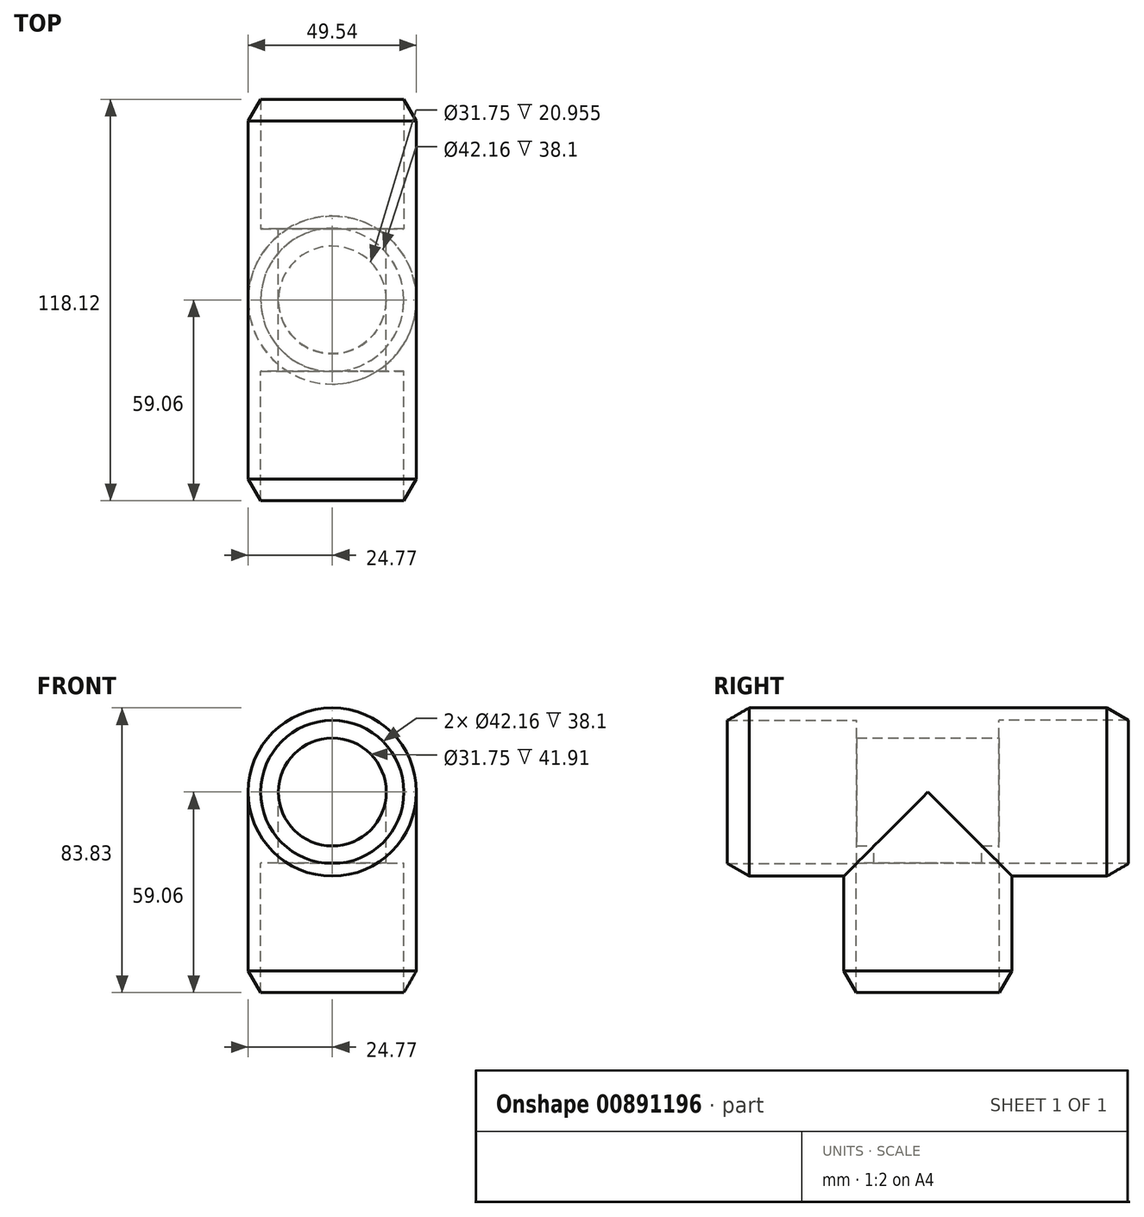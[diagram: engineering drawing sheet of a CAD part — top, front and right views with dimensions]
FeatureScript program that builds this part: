
annotation { "Feature Type Name" : "Feature", "Feature Type Description" : "" }
export const myFeature = defineFeature(function(context is Context, id is Id, definition is map)
    precondition{}
    {
        {
            var Q0;
            Q0=qCreatedBy(makeId("Right.planeOp"),FACE);
            var sketch = newSketch(context, id + "F0", { "sketchPlane" : qUnion([Q0])});
            skLineSegment(sketch, "E0", {"start": v(-59.06, 21.08) * mm, "end": v(-20.96, 21.08) * mm});
            skLineSegment(sketch, "E1", {"start": v(-20.96, 21.08) * mm, "end": v(-20.96, 15.88) * mm});
            skLineSegment(sketch, "E2", {"start": v(-20.96, 15.88) * mm, "end": v(0, 15.88) * mm});
            skLineSegment(sketch, "E3", {"start": v(15.87, 0) * mm, "end": v(15.87, 0) * mm});
            skLineSegment(sketch, "E4", {"start": v(15.87, 0) * mm, "end": v(24.77, 0) * mm});
            skLineSegment(sketch, "E5", {"start": v(24.77, 0) * mm, "end": v(24.77, 0) * mm});
            skLineSegment(sketch, "E6", {"start": v(0, 24.77) * mm, "end": v(-52.68, 24.76) * mm});
            skLineSegment(sketch, "E7", {"start": v(-52.68, 24.76) * mm, "end": v(-59.06, 21.08) * mm});
            skArc(sketch, "E8.filletArc", {"start": v(24.77, 0) * mm, "mid": v(17.51, 17.51) * mm, "end": v(0, 24.77) * mm});
            skArc(sketch, "E9.filletArc", {"start": v(15.88, 0) * mm, "mid": v(11.23, 11.23) * mm, "end": v(0, 15.88) * mm});
            skLineSegment(sketch, "E10", {"start": v(0, 0) * mm, "end": v(0, -11.7) * mm});
            skLineSegment(sketch, "E11", {"start": v(0, 0) * mm, "end": v(10.52, 0) * mm});
            skLineSegment(sketch, "E12", {"start": v(-59.06, 21.08) * mm, "end": v(-59.06, 0) * mm});
            skLineSegment(sketch, "E13", {"start": v(-59.06, 0) * mm, "end": v(15.87, 0) * mm});
            skSolve(sketch);
        }
        {
            var Q0;
            Q0=qCreatedBy(makeId("Right.planeOp"),FACE);
            var sketch = newSketch(context, id + "F1", { "sketchPlane" : qUnion([Q0])});
            skLineSegment(sketch, "E14", {"start": v(-21.08, -59.06) * mm, "end": v(-21.08, -20.96) * mm});
            skLineSegment(sketch, "E15", {"start": v(-21.08, -20.96) * mm, "end": v(-15.88, -20.96) * mm});
            skLineSegment(sketch, "E16", {"start": v(-15.88, -20.96) * mm, "end": v(-15.88, 0) * mm});
            skLineSegment(sketch, "E17", {"start": v(0, 15.88) * mm, "end": v(0, 15.88) * mm});
            skLineSegment(sketch, "E18", {"start": v(0, 15.88) * mm, "end": v(0, 24.77) * mm});
            skLineSegment(sketch, "E19", {"start": v(0, 24.77) * mm, "end": v(0, 24.77) * mm});
            skLineSegment(sketch, "E20", {"start": v(-24.77, 0) * mm, "end": v(-24.76, -52.68) * mm});
            skLineSegment(sketch, "E21", {"start": v(-24.76, -52.68) * mm, "end": v(-21.08, -59.06) * mm});
            skArc(sketch, "E22.filletArc", {"start": v(0, 24.77) * mm, "mid": v(-17.51, 17.51) * mm, "end": v(-24.77, 0) * mm});
            skArc(sketch, "E23.filletArc", {"start": v(0, 15.88) * mm, "mid": v(-11.23, 11.23) * mm, "end": v(-15.88, 0) * mm});
            skLineSegment(sketch, "E24", {"start": v(0, 36.04) * mm, "end": v(0, 0) * mm});
            skLineSegment(sketch, "E25", {"start": v(-2.18, 0) * mm, "end": v(0, 0) * mm});
            skLineSegment(sketch, "E26", {"start": v(-21.08, -59.06) * mm, "end": v(0, -59.06) * mm});
            skLineSegment(sketch, "E27", {"start": v(0, -59.06) * mm, "end": v(0, 15.88) * mm});
            skSolve(sketch);
        }
        {
            var Q0;
            Q0=qCreatedBy(makeId("Right.planeOp"),FACE);
            var sketch = newSketch(context, id + "F2", { "sketchPlane" : qUnion([Q0])});
            skLineSegment(sketch, "E28", {"start": v(59.06, -21.08) * mm, "end": v(20.96, -21.08) * mm});
            skLineSegment(sketch, "E29", {"start": v(20.96, -21.08) * mm, "end": v(20.96, -15.88) * mm});
            skLineSegment(sketch, "E30", {"start": v(20.96, -15.88) * mm, "end": v(0, -15.88) * mm});
            skLineSegment(sketch, "E31", {"start": v(-15.87, 0) * mm, "end": v(-15.87, 0) * mm});
            skLineSegment(sketch, "E32", {"start": v(-15.87, 0) * mm, "end": v(-24.77, 0) * mm});
            skLineSegment(sketch, "E33", {"start": v(-24.77, 0) * mm, "end": v(-24.77, 0) * mm});
            skLineSegment(sketch, "E34", {"start": v(0, -24.77) * mm, "end": v(52.68, -24.76) * mm});
            skLineSegment(sketch, "E35", {"start": v(52.68, -24.77) * mm, "end": v(59.06, -21.08) * mm});
            skArc(sketch, "E36.filletArc", {"start": v(-24.77, 0) * mm, "mid": v(-17.51, -17.51) * mm, "end": v(0, -24.77) * mm});
            skArc(sketch, "E37.filletArc", {"start": v(-15.88, 0) * mm, "mid": v(-11.23, -11.23) * mm, "end": v(0, -15.88) * mm});
            skLineSegment(sketch, "E38", {"start": v(0, 2.6) * mm, "end": v(0, 0) * mm});
            skLineSegment(sketch, "E39", {"start": v(0, 0) * mm, "end": v(10.52, 0) * mm});
            skLineSegment(sketch, "E40", {"start": v(59.06, -21.08) * mm, "end": v(59.06, 0) * mm});
            skLineSegment(sketch, "E41", {"start": v(59.06, 0) * mm, "end": v(-15.87, 0) * mm});
            skSolve(sketch);
        }
        {
            var Q0;
            Q0=qSketchRegion(id+"F0",true);
            var Q1;
            Q1=sQuery(id+"F0.wireOp",EDGE,"E13");
            revolve(context, id + "F3", {"surfaceOperationType" : NewSurfaceOperationType.NEW, "entities" : qUnion([Q0]), "axis" : qUnion([Q1]), "revolveType" : RevolveType.FULL});
        }
        {
            var Q0;
            Q0=qSketchRegion(id+"F1",true);
            var Q1;
            Q1=sQuery(id+"F1.wireOp",EDGE,"E27");
            revolve(context, id + "F4", {"operationType" : NewBodyOperationType.ADD, "surfaceOperationType" : NewSurfaceOperationType.NEW, "entities" : qUnion([Q0]), "axis" : qUnion([Q1]), "revolveType" : RevolveType.FULL});
        }
        {
            var Q0;
            Q0=qSketchRegion(id+"F2",true);
            var Q1;
            Q1=sQuery(id+"F2.wireOp",EDGE,"E41");
            revolve(context, id + "F5", {"operationType" : NewBodyOperationType.ADD, "surfaceOperationType" : NewSurfaceOperationType.NEW, "entities" : qUnion([Q0]), "axis" : qUnion([Q1]), "revolveType" : RevolveType.FULL});
        }
        {
            var Q0;
            Q0=makeQuery(id+"F0.imprint","IMPRINT",FACE,{"disambiguationData":[TD([[makeQuery(id+"F0.imprint","IMPRINT",EDGE,{"derivedFrom":sQuery(id+"F0.wireOp",EDGE,"E0")}),-1.0]])]});
            var Q1;
            Q1=sQuery(id+"F0.wireOp",EDGE,"E13");
            revolve(context, id + "F6", {"operationType" : NewBodyOperationType.REMOVE, "surfaceOperationType" : NewSurfaceOperationType.NEW, "entities" : qUnion([Q0]), "axis" : qUnion([Q1]), "revolveType" : RevolveType.FULL, "oppositeDirection" : true});
        }
        {
            var Q0;
            Q0=makeQuery(id+"F1.imprint","IMPRINT",FACE,{"disambiguationData":[TD([[makeQuery(id+"F1.imprint","IMPRINT",EDGE,{"derivedFrom":sQuery(id+"F1.wireOp",EDGE,"E14")}),-1.0]])]});
            var Q1;
            Q1=sQuery(id+"F1.wireOp",EDGE,"E27");
            revolve(context, id + "F7", {"operationType" : NewBodyOperationType.REMOVE, "surfaceOperationType" : NewSurfaceOperationType.NEW, "entities" : qUnion([Q0]), "axis" : qUnion([Q1]), "revolveType" : RevolveType.FULL, "oppositeDirection" : true});
        }
        {
            var Q0;
            Q0=makeQuery(id+"F2.imprint","IMPRINT",FACE,{"disambiguationData":[TD([[makeQuery(id+"F2.imprint","IMPRINT",EDGE,{"derivedFrom":sQuery(id+"F2.wireOp",EDGE,"E28")}),-1.0]])]});
            var Q1;
            Q1=sQuery(id+"F2.wireOp",EDGE,"E41");
            revolve(context, id + "F8", {"operationType" : NewBodyOperationType.REMOVE, "surfaceOperationType" : NewSurfaceOperationType.NEW, "entities" : qUnion([Q0]), "axis" : qUnion([Q1]), "revolveType" : RevolveType.FULL, "oppositeDirection" : true});
        }
    });
